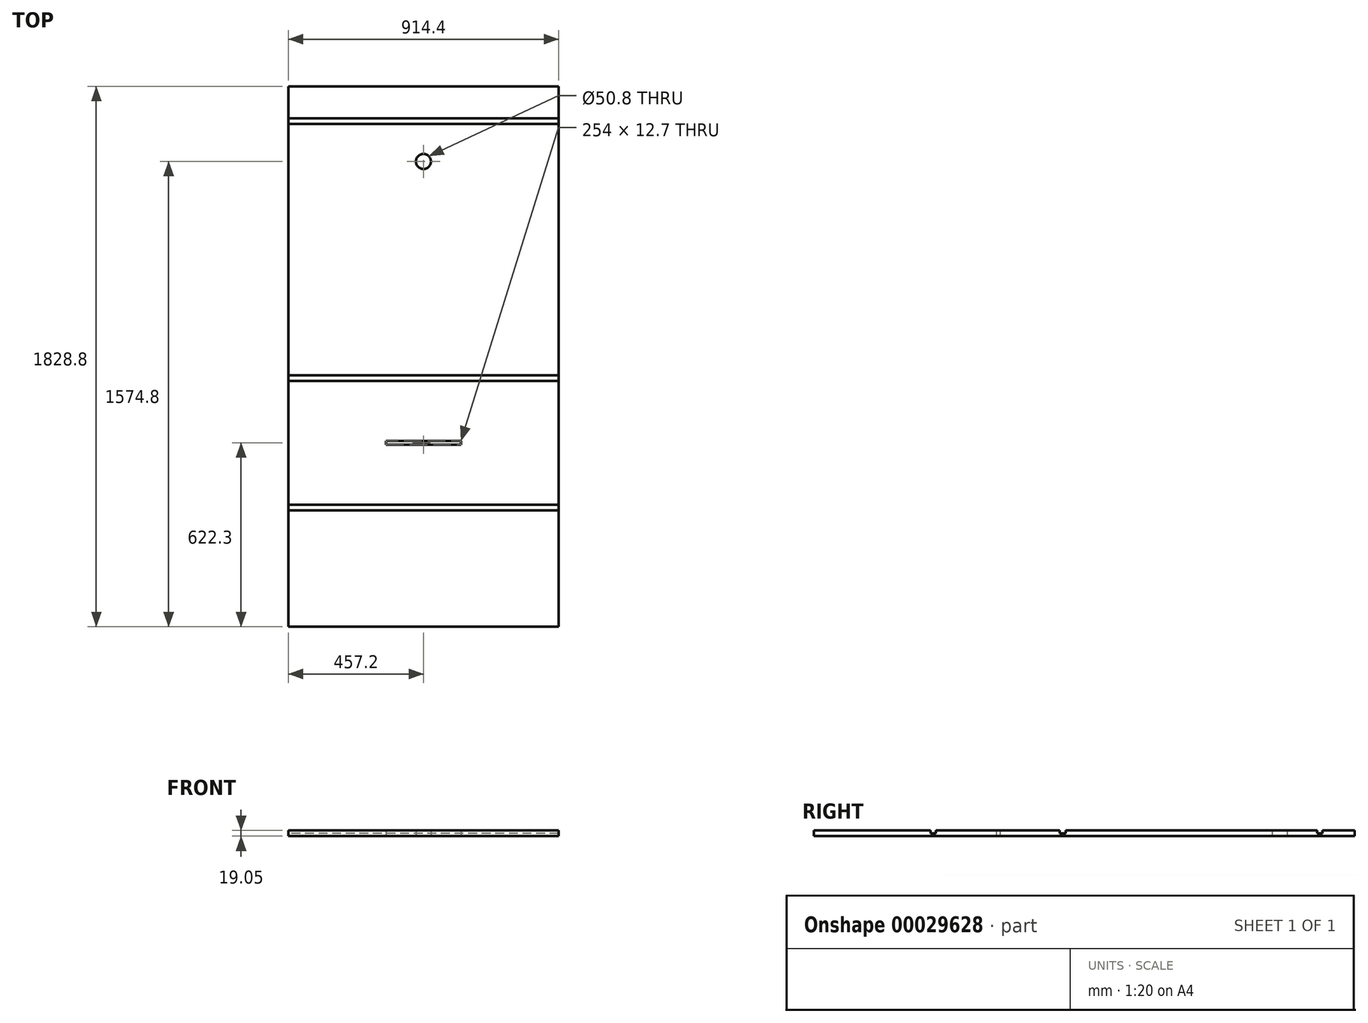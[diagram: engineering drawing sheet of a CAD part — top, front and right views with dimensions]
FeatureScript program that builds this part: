
annotation { "Feature Type Name" : "Feature", "Feature Type Description" : "" }
export const myFeature = defineFeature(function(context is Context, id is Id, definition is map)
    precondition{}
    {
        {
            var Q0;
            Q0=qCreatedBy(makeId("Top.planeOp"),FACE);
            var sketch = newSketch(context, id + "F0", { "sketchPlane" : qUnion([Q0])});
            skLineSegment(sketch, "E0.bottom", {"start": v(0, 0) * mm, "end": v(914.4, 0) * mm});
            skLineSegment(sketch, "E0.top", {"start": v(0, 1828.8) * mm, "end": v(914.4, 1828.8) * mm});
            skLineSegment(sketch, "E0.left", {"start": v(0, 0) * mm, "end": v(0, 1828.8) * mm});
            skLineSegment(sketch, "E0.right", {"start": v(914.4, 0) * mm, "end": v(914.4, 1828.8) * mm});
            skPoint(sketch, "E1", {"position": v(457.2, 0) * mm});
            skPoint(sketch, "E2", {"position": v(457.2, 622.3) * mm});
            skLineSegment(sketch, "E3", {"start": v(457.2, 622.3) * mm, "end": v(584.2, 622.3) * mm});
            skLineSegment(sketch, "E4", {"start": v(457.2, 622.3) * mm, "end": v(330.2, 622.3) * mm});
            skLineSegment(sketch, "E5", {"start": v(330.2, 622.3) * mm, "end": v(330.2, 628.65) * mm});
            skLineSegment(sketch, "E6", {"start": v(584.2, 622.3) * mm, "end": v(584.2, 615.95) * mm});
            skLineSegment(sketch, "E7.bottom", {"start": v(330.2, 628.65) * mm, "end": v(584.2, 628.65) * mm});
            skLineSegment(sketch, "E7.top", {"start": v(330.2, 615.95) * mm, "end": v(584.2, 615.95) * mm});
            skLineSegment(sketch, "E7.left", {"start": v(330.2, 628.65) * mm, "end": v(330.2, 615.95) * mm});
            skLineSegment(sketch, "E7.right", {"start": v(584.2, 628.65) * mm, "end": v(584.2, 615.95) * mm});
            skLineSegment(sketch, "E8", {"start": v(457.2, 615.95) * mm, "end": v(457.2, 412.75) * mm});
            skLineSegment(sketch, "E9", {"start": v(457.2, 628.65) * mm, "end": v(457.2, 831.85) * mm});
            skPoint(sketch, "E10", {"position": v(0, 412.75) * mm});
            skPoint(sketch, "E11", {"position": v(0, 831.85) * mm});
            skLineSegment(sketch, "E12.bottom", {"start": v(0, 412.75) * mm, "end": v(914.4, 412.75) * mm});
            skLineSegment(sketch, "E12.top", {"start": v(0, 393.7) * mm, "end": v(914.4, 393.7) * mm});
            skLineSegment(sketch, "E12.left", {"start": v(0, 412.75) * mm, "end": v(0, 393.7) * mm});
            skLineSegment(sketch, "E12.right", {"start": v(914.4, 412.75) * mm, "end": v(914.4, 393.7) * mm});
            skLineSegment(sketch, "E13.bottom", {"start": v(0, 831.85) * mm, "end": v(914.4, 831.85) * mm});
            skLineSegment(sketch, "E13.top", {"start": v(0, 850.9) * mm, "end": v(914.4, 850.9) * mm});
            skLineSegment(sketch, "E13.left", {"start": v(0, 831.85) * mm, "end": v(0, 850.9) * mm});
            skLineSegment(sketch, "E13.right", {"start": v(914.4, 831.85) * mm, "end": v(914.4, 850.9) * mm});
            skPoint(sketch, "E14", {"position": v(457.2, 1828.8) * mm});
            skPoint(sketch, "E15", {"position": v(457.2, 1574.8) * mm});
            skPoint(sketch, "E16", {"position": v(457.2, 1701.8) * mm});
            skPoint(sketch, "E17", {"position": v(0, 1701.8) * mm});
            skLineSegment(sketch, "E18.bottom", {"start": v(0, 1701.8) * mm, "end": v(914.4, 1701.8) * mm});
            skLineSegment(sketch, "E18.top", {"start": v(0, 1720.85) * mm, "end": v(914.4, 1720.85) * mm});
            skLineSegment(sketch, "E18.left", {"start": v(0, 1701.8) * mm, "end": v(0, 1720.85) * mm});
            skLineSegment(sketch, "E18.right", {"start": v(914.4, 1701.8) * mm, "end": v(914.4, 1720.85) * mm});
            skCircle(sketch, "E19", {"center": v(457.2, 1574.8) * mm, "radius": 25.4 * mm});
            skSolve(sketch);
        }
        {
            var Q0;
            {var subQ0=sQuery(id+"F0.wireOp",EDGE,"E0.top");Q0=makeQuery(id+"F0.imprint","IMPRINT",FACE,{"disambiguationData":[TD([[makeQuery(id+"F0.imprint","IMPRINT",EDGE,{"derivedFrom":subQ0}),-1.0]])]});}
            var Q1;
            {var subQ0=sQuery(id+"F0.wireOp",EDGE,"E13.top");Q1=makeQuery(id+"F0.imprint","IMPRINT",FACE,{"disambiguationData":[TD([[makeQuery(id+"F0.imprint","IMPRINT",EDGE,{"derivedFrom":subQ0}),1.0]])]});}
            var Q2;
            {var subQ4=sQuery(id+"F0.wireOp",EDGE,"E5");Q2=makeQuery(id+"F0.imprint","IMPRINT",FACE,{"disambiguationData":[TD([[makeQuery(id+"F0.imprint","IMPRINT",EDGE,{"derivedFrom":subQ4}),1.0]])]});}
            var Q3;
            {var subQ1=sQuery(id+"F0.wireOp",EDGE,"E6");Q3=makeQuery(id+"F0.imprint","IMPRINT",FACE,{"disambiguationData":[TD([[makeQuery(id+"F0.imprint","IMPRINT",EDGE,{"derivedFrom":subQ1}),1.0]])]});}
            var Q4;
            {var subQ0=sQuery(id+"F0.wireOp",EDGE,"E0.bottom");Q4=makeQuery(id+"F0.imprint","IMPRINT",FACE,{"disambiguationData":[TD([[makeQuery(id+"F0.imprint","IMPRINT",EDGE,{"derivedFrom":subQ0}),1.0]])]});}
            var Q5;
            {var subQ4=sQuery(id+"F0.wireOp",EDGE,"E13.top");Q5=makeQuery(id+"F0.imprint","IMPRINT",FACE,{"disambiguationData":[TD([[makeQuery(id+"F0.imprint","IMPRINT",EDGE,{"derivedFrom":subQ4}),-1.0]])]});}
            var Q6;
            {var subQ6=sQuery(id+"F0.wireOp",EDGE,"E12.top");Q6=makeQuery(id+"F0.imprint","IMPRINT",FACE,{"disambiguationData":[TD([[makeQuery(id+"F0.imprint","IMPRINT",EDGE,{"derivedFrom":subQ6}),1.0]])]});}
            var Q7;
            {var subQ2=sQuery(id+"F0.wireOp",EDGE,"E18.bottom");Q7=makeQuery(id+"F0.imprint","IMPRINT",FACE,{"disambiguationData":[TD([[makeQuery(id+"F0.imprint","IMPRINT",EDGE,{"derivedFrom":subQ2}),1.0]])]});}
            extrude(context, id + "F1", {"entities" : qUnion([Q0, Q1, Q2, Q3, Q4, Q5, Q6, Q7]), "depth" : 9.52 * mm});
        }
        {
            var Q0;
            {var subQ0=sQuery(id+"F0.wireOp",EDGE,"E0.top");Q0=makeQuery(id+"F0.imprint","IMPRINT",FACE,{"disambiguationData":[TD([[makeQuery(id+"F0.imprint","IMPRINT",EDGE,{"derivedFrom":subQ0}),-1.0]])]});}
            var Q1;
            {var subQ0=sQuery(id+"F0.wireOp",EDGE,"E13.top");Q1=makeQuery(id+"F0.imprint","IMPRINT",FACE,{"disambiguationData":[TD([[makeQuery(id+"F0.imprint","IMPRINT",EDGE,{"derivedFrom":subQ0}),1.0]])]});}
            var Q2;
            {var subQ4=sQuery(id+"F0.wireOp",EDGE,"E5");Q2=makeQuery(id+"F0.imprint","IMPRINT",FACE,{"disambiguationData":[TD([[makeQuery(id+"F0.imprint","IMPRINT",EDGE,{"derivedFrom":subQ4}),1.0]])]});}
            var Q3;
            {var subQ1=sQuery(id+"F0.wireOp",EDGE,"E6");Q3=makeQuery(id+"F0.imprint","IMPRINT",FACE,{"disambiguationData":[TD([[makeQuery(id+"F0.imprint","IMPRINT",EDGE,{"derivedFrom":subQ1}),1.0]])]});}
            var Q4;
            {var subQ0=sQuery(id+"F0.wireOp",EDGE,"E0.bottom");Q4=makeQuery(id+"F0.imprint","IMPRINT",FACE,{"disambiguationData":[TD([[makeQuery(id+"F0.imprint","IMPRINT",EDGE,{"derivedFrom":subQ0}),1.0]])]});}
            extrude(context, id + "F2", {"entities" : qUnion([Q0, Q1, Q2, Q3, Q4]), "operationType" : NewBodyOperationType.ADD, "depth" : 19.05 * mm});
        }
    });
